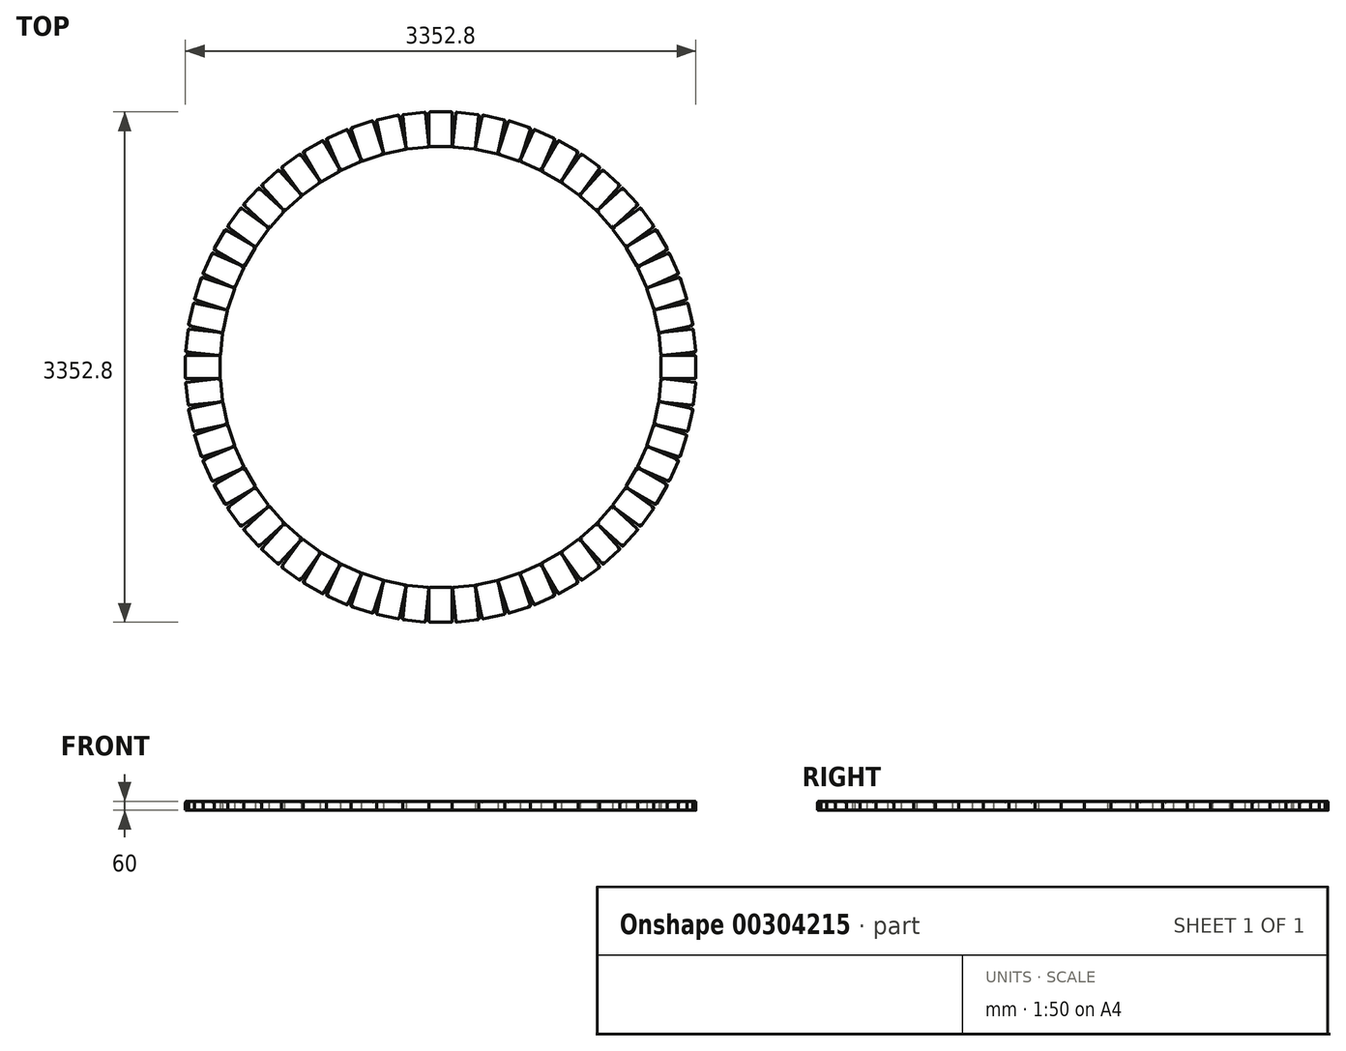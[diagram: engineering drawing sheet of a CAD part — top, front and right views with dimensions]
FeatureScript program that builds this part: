
annotation { "Feature Type Name" : "Feature", "Feature Type Description" : "" }
export const myFeature = defineFeature(function(context is Context, id is Id, definition is map)
    precondition{}
    {
        {
            var Q0;
            Q0=qCreatedBy(makeId("Top.planeOp"),FACE);
            var sketch = newSketch(context, id + "F0", { "sketchPlane" : qUnion([Q0])});
            skCircle(sketch, "E0", {"center": v(0, 0) * mm, "radius": 1447.8 * mm, "construction": true});
            skCircle(sketch, "E1.0", {"center": v(0, 0) * mm, "radius": 1676.4 * mm, "construction": true});
            skLineSegment(sketch, "E2", {"start": v(0, 1447.8) * mm, "end": v(0, -1447.8) * mm, "construction": true});
            skLineSegment(sketch, "E3.bottom", {"start": v(-69.85, -1447.8) * mm, "end": v(69.85, -1447.8) * mm});
            skLineSegment(sketch, "E3.top", {"start": v(-69.85, -1676.4) * mm, "end": v(69.85, -1676.4) * mm});
            skLineSegment(sketch, "E3.left", {"start": v(-76.2, -1454.15) * mm, "end": v(-76.2, -1670.05) * mm});
            skLineSegment(sketch, "E3.right", {"start": v(76.2, -1454.15) * mm, "end": v(76.2, -1670.05) * mm});
            skPoint(sketch, "E4", {"position": v(0, -1447.8) * mm});
            skPoint(sketch, "E5", {"position": v(0, -1676.4) * mm});
            skPoint(sketch, "E6.visualSharp", {"position": v(-76.2, -1676.4) * mm});
            skArc(sketch, "E6.filletArc", {"start": v(-76.2, -1670.05) * mm, "mid": v(-74.34, -1674.54) * mm, "end": v(-69.85, -1676.4) * mm});
            skPoint(sketch, "E7.visualSharp", {"position": v(76.2, -1676.4) * mm});
            skArc(sketch, "E7.filletArc", {"start": v(69.85, -1676.4) * mm, "mid": v(74.34, -1674.54) * mm, "end": v(76.2, -1670.05) * mm});
            skPoint(sketch, "E8.visualSharp", {"position": v(-76.2, -1447.8) * mm});
            skArc(sketch, "E8.filletArc", {"start": v(-69.85, -1447.8) * mm, "mid": v(-74.34, -1449.66) * mm, "end": v(-76.2, -1454.15) * mm});
            skPoint(sketch, "E9.visualSharp", {"position": v(76.2, -1447.8) * mm});
            skArc(sketch, "E9.filletArc", {"start": v(76.2, -1454.15) * mm, "mid": v(74.34, -1449.66) * mm, "end": v(69.85, -1447.8) * mm});
            skLineSegment(sketch, "E10", {"start": v(0, 0) * mm, "end": v(-96.05, -1832.75) * mm, "construction": true});
            skSolve(sketch);
        }
        {
            var Q0;
            Q0=qSketchRegion(id+"F0",true);
            extrude(context, id + "F1", {"entities" : qUnion([Q0]), "depth" : 60 * mm});
        }
        {
            var Q0;
            Q0=makeQuery(id+"F1.opExtrude","CAP_EDGE",EDGE,{"disambiguationData":[OSD([sQuery(id+"F0.wireOp",EDGE,"E3.left")])],"isStart":false});
            fillet(context, id + "F2", {"entities" : qUnion([Q0]), "radius" : 9.52 * mm, "tangentPropagation" : true, "allowEdgeOverflow" : false});
        }
        {
            var Q0;
            Q0=qCreatedBy(makeId("Front.planeOp"),FACE);
            var sketch = newSketch(context, id + "F3", { "sketchPlane" : qUnion([Q0])});
            skLineSegment(sketch, "E11", {"start": v(0, 0) * mm, "end": v(0, 254) * mm, "construction": true});
            skSolve(sketch);
        }
        {
            var Q0;
            Q0=makeQuery(id+"F1.opExtrude","SWEPT_BODY",BODY,{"disambiguationData":[OSD([sQuery(id+"F0.wireOp",EDGE,"E3.bottom"),sQuery(id+"F0.wireOp",EDGE,"E3.top"),sQuery(id+"F0.wireOp",EDGE,"E3.left"),sQuery(id+"F0.wireOp",EDGE,"E3.right"),sQuery(id+"F0.wireOp",EDGE,"E6.filletArc"),sQuery(id+"F0.wireOp",EDGE,"E7.filletArc"),sQuery(id+"F0.wireOp",EDGE,"E8.filletArc"),sQuery(id+"F0.wireOp",EDGE,"E9.filletArc")])]});
            var Q1;
            Q1=sQuery(id+"F3.wireOp",EDGE,"E11");
            circularPattern(context, id + "F4", {"entities" : qUnion([Q0]), "axis" : qUnion([Q1]), "angle" : 360 * degree, "instanceCount" : 60, "equalSpace" : true});
        }
    });
